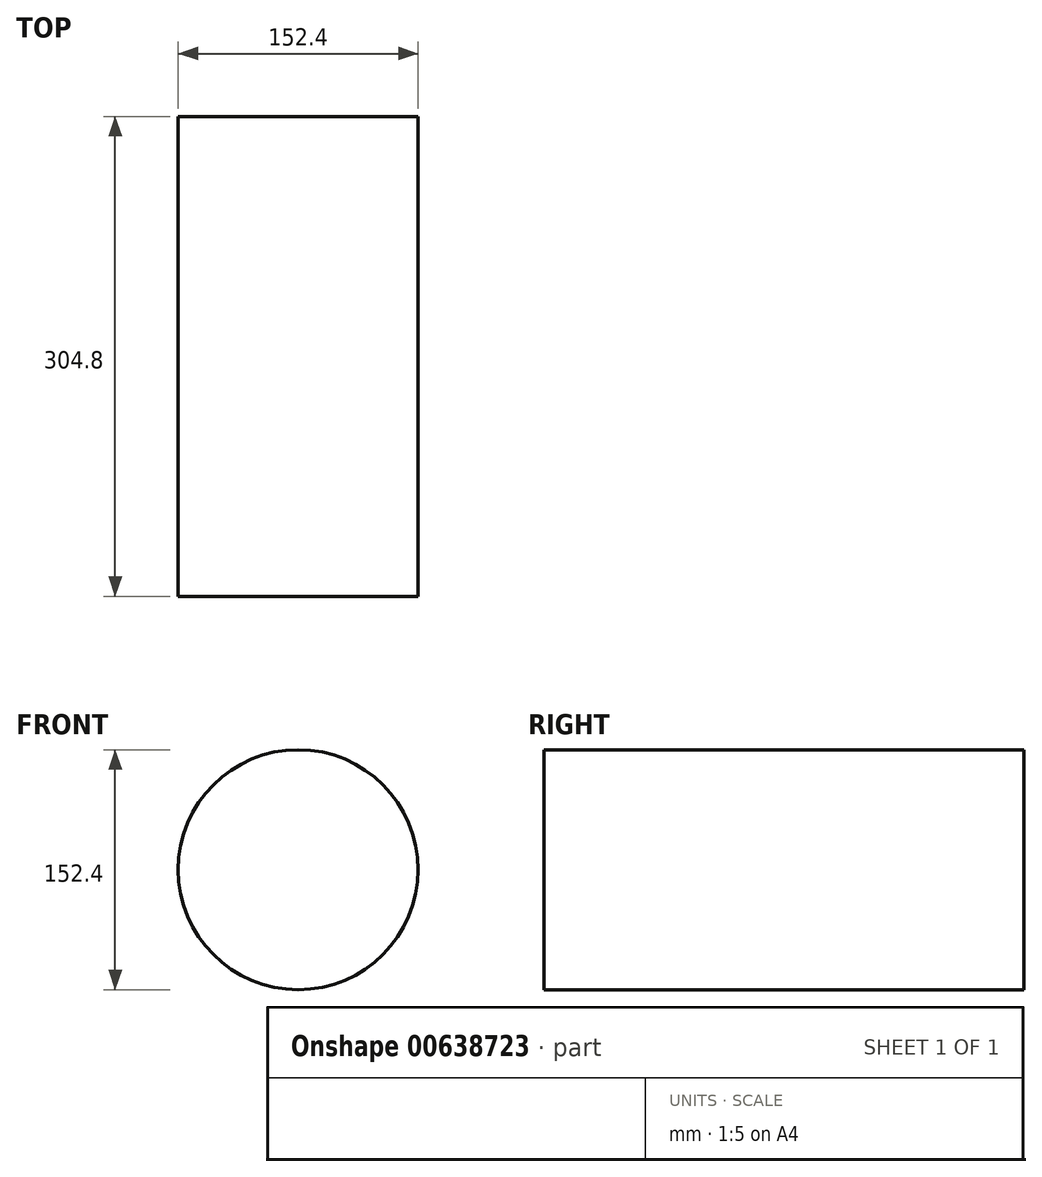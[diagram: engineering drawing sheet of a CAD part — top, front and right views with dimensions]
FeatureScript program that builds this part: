
annotation { "Feature Type Name" : "Feature", "Feature Type Description" : "" }
export const myFeature = defineFeature(function(context is Context, id is Id, definition is map)
    precondition{}
    {
        {
            var Q0;
            Q0=qCreatedBy(makeId("Front.planeOp"),FACE);
            var sketch = newSketch(context, id + "F0", { "sketchPlane" : qUnion([Q0])});
            skCircle(sketch, "E0", {"center": v(0, 0) * mm, "radius": 76.2 * mm});
            skSolve(sketch);
        }
        {
            var Q0;
            Q0=makeQuery(id+"F0.imprint","IMPRINT",FACE,{"disambiguationData":[TD([[makeQuery(id+"F0.imprint","IMPRINT",EDGE,{"derivedFrom":sQuery(id+"F0.wireOp",EDGE,"E0")}),1.0]])]});
            extrude(context, id + "F1", {"entities" : qUnion([Q0]), "depth" : 304.8 * mm, "offsetDistance" : 25.4 * mm});
        }
    });
